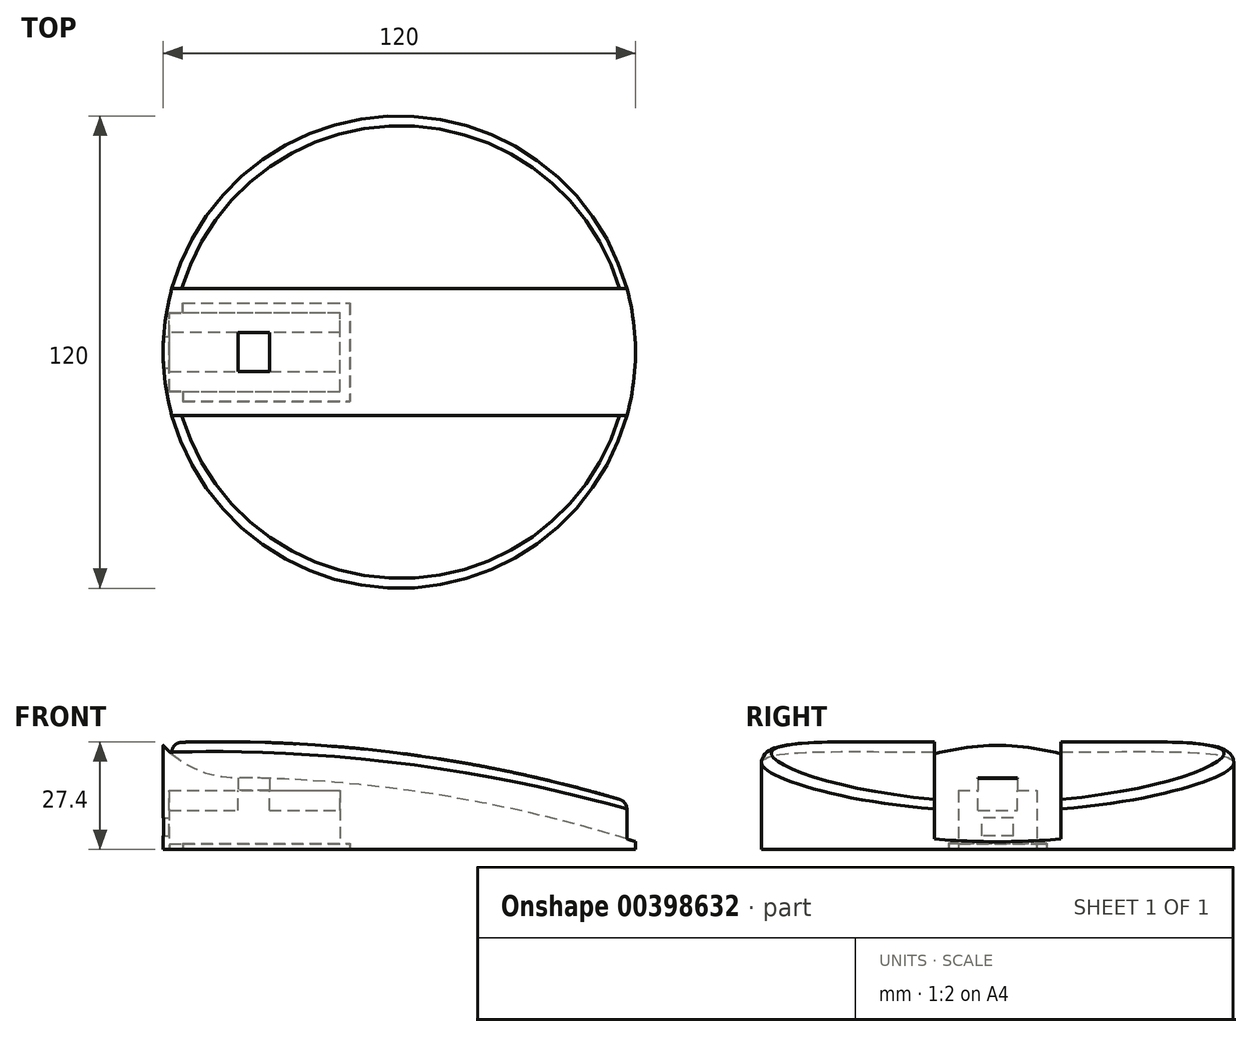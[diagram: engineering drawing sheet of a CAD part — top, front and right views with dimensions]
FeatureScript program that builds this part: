
annotation { "Feature Type Name" : "Feature", "Feature Type Description" : "" }
export const myFeature = defineFeature(function(context is Context, id is Id, definition is map)
    precondition{}
    {
        {
            var Q0;
            Q0=qCreatedBy(makeId("Top.planeOp"),FACE);
            var sketch = newSketch(context, id + "F0", { "sketchPlane" : qUnion([Q0])});
            skCircle(sketch, "E0", {"center": v(0, 0) * mm, "radius": 60 * mm});
            skSolve(sketch);
        }
        {
            var Q0;
            Q0=makeQuery(id+"F0.imprint","IMPRINT",FACE,{"disambiguationData":[TD([[makeQuery(id+"F0.imprint","IMPRINT",EDGE,{"derivedFrom":sQuery(id+"F0.wireOp",EDGE,"E0")}),1.0]])]});
            extrude(context, id + "F1", {"entities" : qUnion([Q0]), "depth" : 40 * mm});
        }
        {
            var Q0;
            Q0=qCreatedBy(makeId("Front.planeOp"),FACE);
            var sketch = newSketch(context, id + "F2", { "sketchPlane" : qUnion([Q0])});
            skArc(sketch, "E1", {"start": v(60, 2) * mm, "mid": v(0.7, 15.23) * mm, "end": v(-60, 18) * mm});
            skArc(sketch, "E2.0", {"start": v(60, 11.53) * mm, "mid": v(0.66, 24.41) * mm, "end": v(-60, 27.1) * mm});
            skLineSegment(sketch, "E3", {"start": v(-60, 18) * mm, "end": v(-60, 41.47) * mm});
            skLineSegment(sketch, "E4", {"start": v(-60, 41.47) * mm, "end": v(60, 41.47) * mm});
            skLineSegment(sketch, "E5", {"start": v(60, 41.47) * mm, "end": v(60, 2) * mm});
            skArc(sketch, "E6", {"start": v(-60, 18) * mm, "mid": v(-69.54, 118.6) * mm, "end": v(-31, 212) * mm});
            skArc(sketch, "E7", {"start": v(-65.75, 37.3) * mm, "mid": v(-57, 23.68) * mm, "end": v(-41.75, 18.28) * mm});
            skSolve(sketch);
        }
        {
            var Q0;
            {var subQ0=sQuery(id+"F2.wireOp",EDGE,"E2.0");Q0=makeQuery(id+"F2.imprint","IMPRINT",FACE,{"disambiguationData":[TD([[makeQuery(id+"F2.imprint","IMPRINT",EDGE,{"derivedFrom":subQ0}),-1.0]])]});}
            extrude(context, id + "F3", {"entities" : qUnion([Q0]), "operationType" : NewBodyOperationType.REMOVE, "endBound" : BoundingType.SYMMETRIC, "oppositeDirection" : true, "depth" : 200 * mm});
        }
        {
            var Q0;
            {var subQ3=sQuery(id+"F2.wireOp",EDGE,"E2.0");Q0=makeQuery(id+"F2.imprint","IMPRINT",FACE,{"disambiguationData":[TD([[makeQuery(id+"F2.imprint","IMPRINT",EDGE,{"derivedFrom":subQ3}),1.0]])]});}
            extrude(context, id + "F4", {"entities" : qUnion([Q0]), "operationType" : NewBodyOperationType.REMOVE, "endBound" : BoundingType.SYMMETRIC, "oppositeDirection" : true, "depth" : 32.2 * mm});
        }
        {
            var Q0;
            Q0=makeQuery(id+"F1.opExtrude","CAP_FACE",FACE,{"disambiguationData":[OSD([sQuery(id+"F0.wireOp",EDGE,"E0")])],"isStart":true});
            var sketch = newSketch(context, id + "F5", { "sketchPlane" : qUnion([Q0])});
            skLineSegment(sketch, "E8.bottom", {"start": v(-58.5, 10) * mm, "end": v(-55, 10) * mm});
            skLineSegment(sketch, "E8.top", {"start": v(-58.5, -10) * mm, "end": v(-55, -10) * mm});
            skLineSegment(sketch, "E8.left", {"start": v(-58.5, 10) * mm, "end": v(-58.5, -10) * mm});
            skLineSegment(sketch, "E8.right", {"start": v(-15, 10) * mm, "end": v(-15, -10) * mm});
            skLineSegment(sketch, "E9", {"start": v(-15, 0) * mm, "end": v(0, 0) * mm, "construction": true});
            skLineSegment(sketch, "E10", {"start": v(-55, 10) * mm, "end": v(-55, 12.5) * mm});
            skLineSegment(sketch, "E11", {"start": v(-55, 12.5) * mm, "end": v(-15, 12.5) * mm});
            skLineSegment(sketch, "E12", {"start": v(-15, 12.5) * mm, "end": v(-15, 10) * mm});
            skLineSegment(sketch, "E13.MirrorCS", {"start": v(-55, -12.5) * mm, "end": v(-15, -12.5) * mm});
            skLineSegment(sketch, "E14.MirrorCS", {"start": v(-15, -12.5) * mm, "end": v(-15, -10) * mm});
            skLineSegment(sketch, "E15.MirrorCS", {"start": v(-55, -10) * mm, "end": v(-55, -12.5) * mm});
            skLineSegment(sketch, "E16", {"start": v(-55, 10) * mm, "end": v(-15, 10) * mm});
            skLineSegment(sketch, "E17", {"start": v(-55, -10) * mm, "end": v(-15, -10) * mm});
            skLineSegment(sketch, "E18", {"start": v(-15, 12.5) * mm, "end": v(-12.5, 12.5) * mm});
            skLineSegment(sketch, "E19", {"start": v(-15, -12.5) * mm, "end": v(-12.5, -12.5) * mm});
            skLineSegment(sketch, "E20", {"start": v(-12.5, -12.5) * mm, "end": v(-12.5, 12.5) * mm});
            skSolve(sketch);
        }
        {
            var Q0;
            Q0=makeQuery(id+"F5.imprint","IMPRINT",FACE,{"disambiguationData":[TD([[makeQuery(id+"F5.imprint","IMPRINT",EDGE,{"derivedFrom":sQuery(id+"F5.wireOp",EDGE,"E8.bottom")}),-1.0]])]});
            extrude(context, id + "F6", {"entities" : qUnion([Q0]), "operationType" : NewBodyOperationType.REMOVE, "oppositeDirection" : true, "depth" : 15 * mm});
        }
        {
            var Q0;
            Q0=makeQuery(id+"F6.boolean.opBoolean","COPY",FACE,{"derivedFrom":makeQuery(id+"F6.opExtrude","CAP_FACE",FACE,{"disambiguationData":[OSD([sQuery(id+"F5.wireOp",EDGE,"E8.bottom"),sQuery(id+"F5.wireOp",EDGE,"E8.top"),sQuery(id+"F5.wireOp",EDGE,"E8.left"),sQuery(id+"F5.wireOp",EDGE,"E8.right")])],"isStart":false})});
            var sketch = newSketch(context, id + "F7", { "sketchPlane" : qUnion([Q0])});
            skLineSegment(sketch, "E21.bottom", {"start": v(-33, -5) * mm, "end": v(-41, -5) * mm});
            skLineSegment(sketch, "E21.top", {"start": v(-33, 5) * mm, "end": v(-41, 5) * mm});
            skLineSegment(sketch, "E21.left", {"start": v(-33, -5) * mm, "end": v(-33, 5) * mm});
            skLineSegment(sketch, "E21.right", {"start": v(-41, -5) * mm, "end": v(-41, 5) * mm});
            skPoint(sketch, "E21.middle", {"position": v(-37, 0) * mm});
            skSolve(sketch);
        }
        {
            var Q0;
            Q0=makeQuery(id+"F7.imprint","IMPRINT",FACE,{"disambiguationData":[TD([[makeQuery(id+"F7.imprint","IMPRINT",EDGE,{"derivedFrom":sQuery(id+"F7.wireOp",EDGE,"E21.bottom")}),-1.0]])]});
            extrude(context, id + "F8", {"entities" : qUnion([Q0]), "operationType" : NewBodyOperationType.REMOVE, "endBound" : BoundingType.THROUGH_ALL, "oppositeDirection" : true, "depth" : 25 * mm});
        }
        {
            var Q0;
            Q0=makeQuery(id+"F6.boolean.opBoolean","COPY",FACE,{"derivedFrom":makeQuery(id+"F6.opExtrude","CAP_FACE",FACE,{"disambiguationData":[OSD([sQuery(id+"F5.wireOp",EDGE,"E8.bottom"),sQuery(id+"F5.wireOp",EDGE,"E8.top"),sQuery(id+"F5.wireOp",EDGE,"E8.left"),sQuery(id+"F5.wireOp",EDGE,"E8.right"),sQuery(id+"F5.wireOp",EDGE,"NnwXaxv1-B9P7-EYR6-hBOz-B7lYGoeBAW6h.bottom"),sQuery(id+"F5.wireOp",EDGE,"NnwXaxv1-B9P7-EYR6-hBOz-B7lYGoeBAW6h.top"),sQuery(id+"F5.wireOp",EDGE,"NnwXaxv1-B9P7-EYR6-hBOz-B7lYGoeBAW6h.left"),sQuery(id+"F5.wireOp",EDGE,"NnwXaxv1-B9P7-EYR6-hBOz-B7lYGoeBAW6h.right")])],"isStart":false})});
            var sketch = newSketch(context, id + "F9", { "sketchPlane" : qUnion([Q0])});
            skLineSegment(sketch, "E22", {"start": v(-58.5, 5) * mm, "end": v(-15, 5) * mm});
            skLineSegment(sketch, "E23", {"start": v(-15, 5) * mm, "end": v(-15, -5) * mm});
            skLineSegment(sketch, "E24", {"start": v(-15, -5) * mm, "end": v(-58.5, -5) * mm});
            skLineSegment(sketch, "E25", {"start": v(-58.5, -5) * mm, "end": v(-58.5, 5) * mm});
            skSolve(sketch);
        }
        {
            var Q0;
            {var subQ2=sQuery(id+"F9.wireOp",EDGE,"E25");Q0=makeQuery(id+"F9.imprint","IMPRINT",FACE,{"disambiguationData":[TD([[makeQuery(id+"F9.imprint","IMPRINT",EDGE,{"derivedFrom":subQ2}),1.0]])]});}
            var Q1;
            {var subQ2=sQuery(id+"F9.wireOp",EDGE,"E25");Q1=makeQuery(id+"F9.imprint","IMPRINT",FACE,{"disambiguationData":[TD([[makeQuery(id+"F9.imprint","IMPRINT",EDGE,{"derivedFrom":subQ2}),1.0]])]});}
            var Q2;
            {var subQ2=sQuery(id+"F9.wireOp",EDGE,"E23");Q2=makeQuery(id+"F9.imprint","IMPRINT",FACE,{"disambiguationData":[TD([[makeQuery(id+"F9.imprint","IMPRINT",EDGE,{"derivedFrom":subQ2}),-1.0]])]});}
            extrude(context, id + "F10", {"entities" : qUnion([Q0, Q1, Q2]), "operationType" : NewBodyOperationType.ADD, "depth" : 5 * mm});
        }
        {
            var Q0;
            Q0=makeQuery(id+"F6.boolean.opBoolean","COPY",FACE,{"derivedFrom":makeQuery(id+"F6.opExtrude","SWEPT_FACE",FACE,{"disambiguationData":[OSD([sQuery(id+"F5.wireOp",EDGE,"E8.left")])]})});
            var sketch = newSketch(context, id + "F11", { "sketchPlane" : qUnion([Q0])});
            skLineSegment(sketch, "E26.bottom", {"start": v(4, 3.5) * mm, "end": v(-4, 3.5) * mm});
            skLineSegment(sketch, "E26.top", {"start": v(4, 8) * mm, "end": v(-4, 8) * mm});
            skLineSegment(sketch, "E26.left", {"start": v(4, 3.5) * mm, "end": v(4, 8) * mm});
            skLineSegment(sketch, "E26.right", {"start": v(-4, 3.5) * mm, "end": v(-4, 8) * mm});
            skPoint(sketch, "E26.middle", {"position": v(0, 5.75) * mm});
            skPoint(sketch, "E26.middle.positionSnap0", {"position": v(0, 10) * mm});
            skPoint(sketch, "E26.centerSnap0", {"position": v(0, 10) * mm});
            skSolve(sketch);
        }
        {
            var Q0;
            Q0=makeQuery(id+"F11.imprint","IMPRINT",FACE,{"disambiguationData":[TD([[makeQuery(id+"F11.imprint","IMPRINT",EDGE,{"derivedFrom":sQuery(id+"F11.wireOp",EDGE,"E26.bottom")}),-1.0]])]});
            extrude(context, id + "F12", {"entities" : qUnion([Q0]), "operationType" : NewBodyOperationType.REMOVE, "endBound" : BoundingType.THROUGH_ALL, "oppositeDirection" : true, "depth" : 25 * mm});
        }
        {
            var Q0;
            {var subQ2=sQuery(id+"F5.wireOp",EDGE,"E10");Q0=makeQuery(id+"F5.imprint","IMPRINT",FACE,{"disambiguationData":[TD([[makeQuery(id+"F5.imprint","IMPRINT",EDGE,{"derivedFrom":subQ2}),-1.0]])]});}
            var Q1;
            Q1=makeQuery(id+"F5.imprint","IMPRINT",FACE,{"disambiguationData":[TD([[makeQuery(id+"F5.imprint","IMPRINT",EDGE,{"derivedFrom":sQuery(id+"F5.wireOp",EDGE,"E13.MirrorCS")}),1.0]])]});
            var Q2;
            Q2=makeQuery(id+"F5.imprint","IMPRINT",FACE,{"disambiguationData":[TD([[makeQuery(id+"F5.imprint","IMPRINT",EDGE,{"derivedFrom":sQuery(id+"F5.wireOp",EDGE,"E8.right")}),1.0]])]});
            extrude(context, id + "F13", {"entities" : qUnion([Q0, Q1, Q2]), "operationType" : NewBodyOperationType.REMOVE, "oppositeDirection" : true, "depth" : 1.6 * mm});
        }
        {
            var Q0;
            Q0=makeQuery(id+"F5.imprint","IMPRINT",FACE,{"disambiguationData":[TD([[makeQuery(id+"F5.imprint","IMPRINT",EDGE,{"derivedFrom":sQuery(id+"F5.wireOp",EDGE,"E8.bottom")}),1.0]])]});
            var sketch = newSketch(context, id + "F14", { "sketchPlane" : qUnion([Q0])});
            skLineSegment(sketch, "E27.0", {"start": v(-54.9, 9.9) * mm, "end": v(-54.9, 12.4) * mm});
            skLineSegment(sketch, "E27.1", {"start": v(-58.4, 9.9) * mm, "end": v(-54.9, 9.9) * mm});
            skLineSegment(sketch, "E27.2", {"start": v(-54.9, 12.4) * mm, "end": v(-15, 12.4) * mm});
            skLineSegment(sketch, "E27.3", {"start": v(-58.4, 9.9) * mm, "end": v(-58.4, -9.9) * mm});
            skLineSegment(sketch, "E27.4", {"start": v(-58.4, -9.9) * mm, "end": v(-54.9, -9.9) * mm});
            skLineSegment(sketch, "E27.5", {"start": v(-54.9, -9.9) * mm, "end": v(-54.9, -12.4) * mm});
            skLineSegment(sketch, "E27.6", {"start": v(-15, 12.4) * mm, "end": v(-12.6, 12.4) * mm});
            skLineSegment(sketch, "E27.7", {"start": v(-12.6, -12.4) * mm, "end": v(-12.6, 12.4) * mm});
            skLineSegment(sketch, "E27.8", {"start": v(-15, -12.4) * mm, "end": v(-12.6, -12.4) * mm});
            skLineSegment(sketch, "E27.9", {"start": v(-54.9, -12.4) * mm, "end": v(-15, -12.4) * mm});
            skSolve(sketch);
        }
        {
            var Q0;
            Q0 = qSketchRegion(id + "F14", true);
            extrude(context, id + "F15", {"entities" : qUnion([Q0]), "oppositeDirection" : true, "depth" : 1.5 * mm});
        }
        {
            var Q0;
            {var subQ0=makeQuery(id+"F1.opExtrude","SWEPT_FACE",FACE,{"disambiguationData":[OSD([sQuery(id+"F0.wireOp",EDGE,"E0")])]});var subQ1=sQuery(id+"F2.wireOp",EDGE,"E2.0");var subQ2=makeQuery(id+"F3.opExtrude","SWEPT_FACE",FACE,{"disambiguationData":[OSD([subQ1])]});Q0=makeQuery(id+"F4.boolean.opBoolean","SPLIT",EDGE,{"disambiguationData":[TD([makeQuery(id+"F4.opExtrude","CAP_FACE",FACE,{"disambiguationData":[OSD([sQuery(id+"F2.wireOp",EDGE,"E1"),subQ1,sQuery(id+"F2.wireOp",EDGE,"E3"),sQuery(id+"F2.wireOp",EDGE,"E5"),sQuery(id+"F2.wireOp",EDGE,"E7")])],"isStart":true})])],"derivedFrom":makeQuery(id+"F3.boolean.opBoolean","INTERSECT",EDGE,{"derivedFrom":[subQ0,subQ2]})});}
            var Q1;
            {var subQ0=makeQuery(id+"F1.opExtrude","SWEPT_FACE",FACE,{"disambiguationData":[OSD([sQuery(id+"F0.wireOp",EDGE,"E0")])]});var subQ1=sQuery(id+"F2.wireOp",EDGE,"E2.0");var subQ2=makeQuery(id+"F3.opExtrude","SWEPT_FACE",FACE,{"disambiguationData":[OSD([subQ1])]});Q1=makeQuery(id+"F4.boolean.opBoolean","SPLIT",EDGE,{"disambiguationData":[TD([makeQuery(id+"F4.opExtrude","CAP_FACE",FACE,{"disambiguationData":[OSD([sQuery(id+"F2.wireOp",EDGE,"E1"),subQ1,sQuery(id+"F2.wireOp",EDGE,"E3"),sQuery(id+"F2.wireOp",EDGE,"E5"),sQuery(id+"F2.wireOp",EDGE,"E7")])],"isStart":false})])],"derivedFrom":makeQuery(id+"F3.boolean.opBoolean","INTERSECT",EDGE,{"derivedFrom":[subQ0,subQ2]})});}
            fillet(context, id + "F16", {"entities" : qUnion([Q0, Q1]), "radius" : 2.5 * mm, "tangentPropagation" : true, "allowEdgeOverflow" : false});
        }
    });
